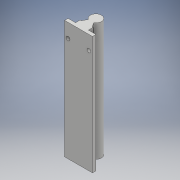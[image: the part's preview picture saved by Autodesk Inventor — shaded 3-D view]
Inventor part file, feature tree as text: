
AUTODESK INVENTOR PART (.ipt)
format: ipt  version: 2018 (Build 220112000, 112)  size: 129,024 bytes
history: native  units: mm
features: sketch x2, other x1, extrude x1, hole x1
ambient origin geometry x8: Origin, YZ Plane, XZ Plane, XY Plane, X Axis, Y Axis, Z Axis, Center Point
bodies: Body1 (feature_tree)
feature tree (5):
  other  "Sólido1"
  extrude  "Extrusão1"  Depth=25.0mm
  hole  "Furo1"  [1 undecoded]
  sketch  "Esboço1"  dims[d6=16.0mm d7=25.0mm]
  sketch  "Esboço3"  dims[d8=18.5mm d9=11.7mm d10=8.0mm d11=30.0deg d12=30.0deg d13=5.0mm d14=40.0mm d15=170.0mm d16=0.0mm d18=15.0mm d19=15.0mm d20=5.5mm d21=5.5mm d22=20.0mm d28=5.5mm d29=6.0mm d30=4.0mm d31=2.0mm d32=90.0deg d33=8.0mm d34=20.594885mm]
note: 1 required parameter value undecoded (feature->parameter linkage not recoverable at this tier; creation-order binding heuristic only, values carry confidence <= 0.55)
